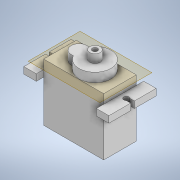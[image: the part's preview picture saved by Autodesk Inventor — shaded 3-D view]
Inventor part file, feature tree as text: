
AUTODESK INVENTOR PART (.ipt)
format: ipt  version: 2021.1 (Build 251245010, 245A)  size: 182,272 bytes
history: native  units: in
note: dims shown in document units (in); Inventor stores cm internally (conversion verified against a paired STEP export)
features: extrude x6, sketch x6, plane x5, mirror x2
ambient origin geometry x8: Origin, YZ Plane, XZ Plane, XY Plane, X Axis, Y Axis, Z Axis, Center Point
bodies: Solid1 (feature_tree)
feature tree (19):
  extrude  "Extrusion1"  Depth=0.4921in
  plane  "Work Plane3"
  plane  "Work Plane4"
  plane  "Work Plane5"
  extrude  "Extrusion2"  Depth=0.8661in
  mirror  "Mirror1"
  plane  "Work Plane6"
  extrude  "Extrusion3"  Depth=0.1102in
  extrude  "Extrusion4"  Depth=0.1102in
  extrude  "Extrusion5"  Depth=0.4331in
  extrude  "Extrusion6"  Depth=0.0984in
  mirror  "Mirror2"
  sketch  "Sketch1"  dims[d0=0.9055in d1=0.4921in]
  plane  "Work Plane2"
  sketch  "Sketch2"  dims[d2=0.8661in d3=0.0in d4=0.4528in d5=-0.9055in d6=0.1969in d7=0.2461in]
  sketch  "Sketch3"  dims[d8=0.6299in d9=0.1102in]
  sketch  "Sketch4"  dims[d10=0.0984in d11=0.1102in]
  sketch  "Sketch5"  dims[d12=0.189in d13=0.0in d14=0.4331in]
  sketch  "Sketch6"  dims[d15=0.4173in d16=0.4803in d17=0.0787in d18=0.1378in d19=0.0in d20=0.1575in d21=0.126in d22=0.0in d23=0.126in d24=0.0in d25=0.0787in d26=0.0984in d27=0.0in]
